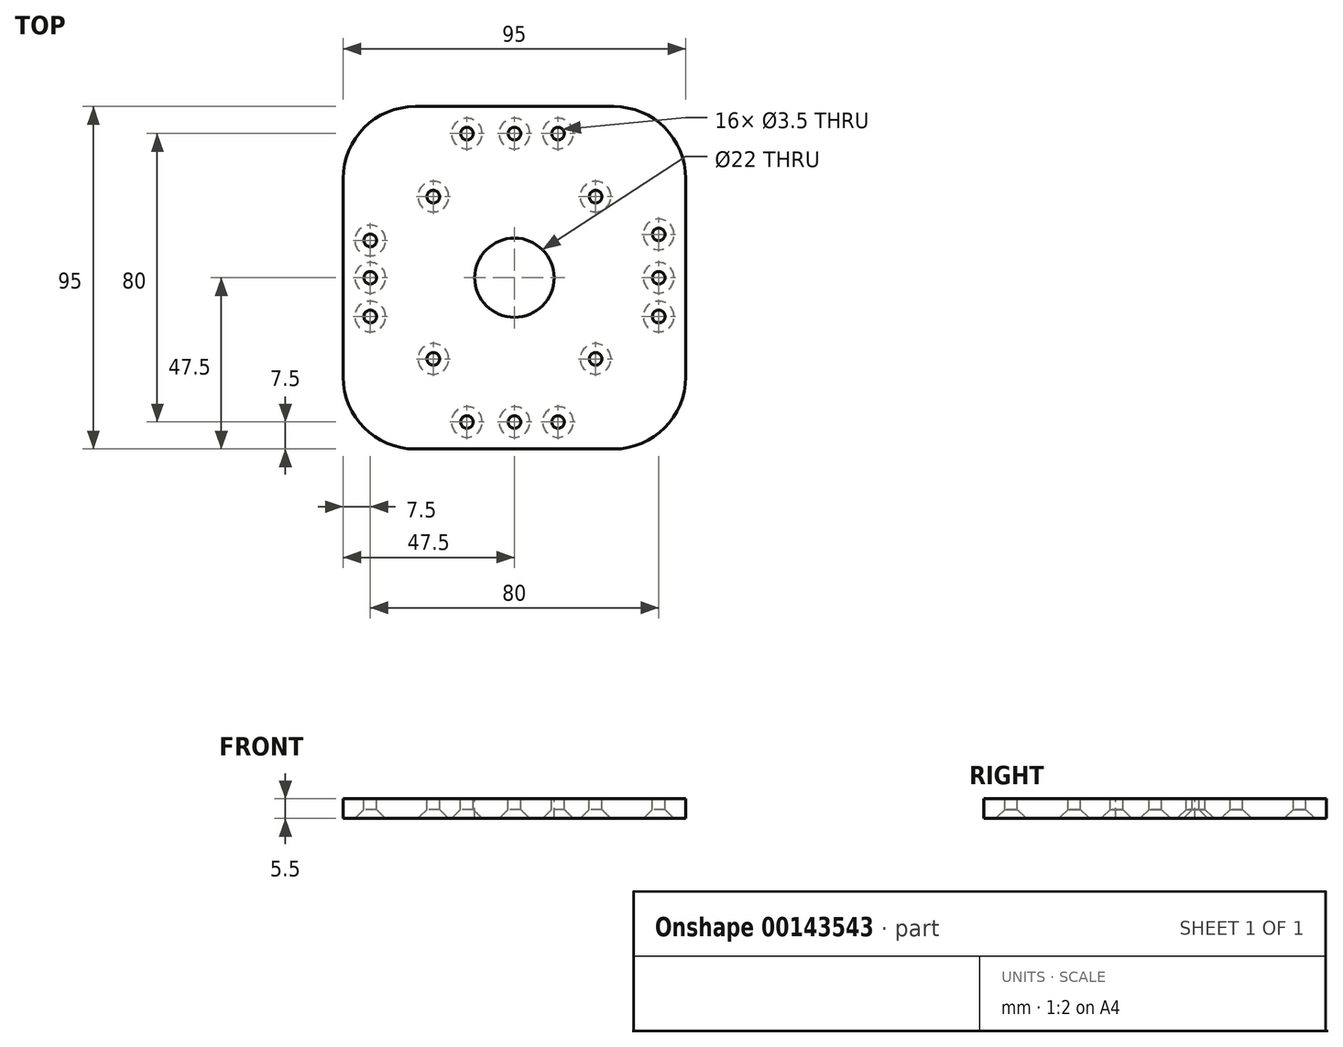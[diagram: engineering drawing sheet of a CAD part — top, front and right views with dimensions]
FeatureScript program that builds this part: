
annotation { "Feature Type Name" : "Feature", "Feature Type Description" : "" }
export const myFeature = defineFeature(function(context is Context, id is Id, definition is map)
    precondition{}
    {
        {
            var Q0;
            Q0=qCreatedBy(makeId("Top.planeOp"),FACE);
            var sketch = newSketch(context, id + "F0", { "sketchPlane" : qUnion([Q0])});
            skLineSegment(sketch, "E0.bottom", {"start": v(-47.5, 47.5) * mm, "end": v(47.5, 47.5) * mm});
            skLineSegment(sketch, "E0.top", {"start": v(-47.5, -47.5) * mm, "end": v(47.5, -47.5) * mm});
            skLineSegment(sketch, "E0.left", {"start": v(-47.5, 47.5) * mm, "end": v(-47.5, -47.5) * mm});
            skLineSegment(sketch, "E0.right", {"start": v(47.5, 47.5) * mm, "end": v(47.5, -47.5) * mm});
            skSolve(sketch);
        }
        {
            var Q0;
            Q0=makeQuery(id+"F0.imprint","IMPRINT",FACE,{"disambiguationData":[TD([[makeQuery(id+"F0.imprint","IMPRINT",EDGE,{"derivedFrom":sQuery(id+"F0.wireOp",EDGE,"E0.bottom")}),-1.0]])]});
            extrude(context, id + "F1", {"entities" : qUnion([Q0]), "depth" : 5.5 * mm});
        }
        {
            var Q0;
            Q0=makeQuery(id+"F1.opExtrude","SWEPT_EDGE",EDGE,{"disambiguationData":[OSD([sQuery(id+"F0.wireOp",EDGE,"E0.top"),sQuery(id+"F0.wireOp",EDGE,"E0.right")])]});
            var Q1;
            Q1=makeQuery(id+"F1.opExtrude","SWEPT_EDGE",EDGE,{"disambiguationData":[OSD([sQuery(id+"F0.wireOp",EDGE,"E0.bottom"),sQuery(id+"F0.wireOp",EDGE,"E0.right")])]});
            var Q2;
            Q2=makeQuery(id+"F1.opExtrude","SWEPT_EDGE",EDGE,{"disambiguationData":[OSD([sQuery(id+"F0.wireOp",EDGE,"E0.bottom"),sQuery(id+"F0.wireOp",EDGE,"E0.left")])]});
            var Q3;
            Q3=makeQuery(id+"F1.opExtrude","SWEPT_EDGE",EDGE,{"disambiguationData":[OSD([sQuery(id+"F0.wireOp",EDGE,"E0.top"),sQuery(id+"F0.wireOp",EDGE,"E0.left")])]});
            fillet(context, id + "F2", {"entities" : qUnion([Q0, Q1, Q2, Q3]), "radius" : 20 * mm, "tangentPropagation" : true, "allowEdgeOverflow" : false});
        }
        {
            var Q0;
            Q0=makeQuery(id+"F1.opExtrude","CAP_FACE",FACE,{"disambiguationData":[OSD([sQuery(id+"F0.wireOp",EDGE,"E0.bottom"),sQuery(id+"F0.wireOp",EDGE,"E0.top"),sQuery(id+"F0.wireOp",EDGE,"E0.left"),sQuery(id+"F0.wireOp",EDGE,"E0.right")])],"isStart":false});
            var sketch = newSketch(context, id + "F3", { "sketchPlane" : qUnion([Q0])});
            skCircle(sketch, "E1", {"center": v(0, 0) * mm, "radius": 11 * mm});
            skPoint(sketch, "E2", {"position": v(0, 40) * mm});
            skPoint(sketch, "E3", {"position": v(-40, 0) * mm});
            skPoint(sketch, "E4", {"position": v(0, -40) * mm});
            skPoint(sketch, "E5", {"position": v(40, 0) * mm});
            skSolve(sketch);
        }
        {
            var Q0;
            Q0 = qSketchRegion(id + "F3", true);
            extrude(context, id + "F4", {"entities" : qUnion([Q0]), "operationType" : NewBodyOperationType.REMOVE, "oppositeDirection" : true, "depth" : 5.5 * mm});
        }
        {
            var Q0;
            Q0=makeQuery(id+"F1.opExtrude","CAP_FACE",FACE,{"disambiguationData":[OSD([sQuery(id+"F0.wireOp",EDGE,"E0.bottom"),sQuery(id+"F0.wireOp",EDGE,"E0.top"),sQuery(id+"F0.wireOp",EDGE,"E0.left"),sQuery(id+"F0.wireOp",EDGE,"E0.right")])],"isStart":true});
            var sketch = newSketch(context, id + "F5", { "sketchPlane" : qUnion([Q0])});
            skPoint(sketch, "E6", {"position": v(0, 40) * mm});
            skPoint(sketch, "E7", {"position": v(40, 0) * mm});
            skPoint(sketch, "E8", {"position": v(-40, 0) * mm});
            skPoint(sketch, "E9", {"position": v(0, -40) * mm});
            skSolve(sketch);
        }
        {
            var Q0;
            Q0=sQuery(id+"F5.wireOp",VERTEX,"E9");
            var Q1;
            Q1=sQuery(id+"F5.wireOp",VERTEX,"E6");
            var Q2;
            Q2=sQuery(id+"F5.wireOp",VERTEX,"E7");
            var Q3;
            Q3=sQuery(id+"F5.wireOp",VERTEX,"E8");
            var Q4;
            Q4=makeQuery(id+"F1.opExtrude","SWEPT_BODY",BODY,{"disambiguationData":[OSD([sQuery(id+"F0.wireOp",EDGE,"E0.bottom"),sQuery(id+"F0.wireOp",EDGE,"E0.top"),sQuery(id+"F0.wireOp",EDGE,"E0.left"),sQuery(id+"F0.wireOp",EDGE,"E0.right")])]});
            hole(context, id + "F6", {"style" : HoleStyle.C_SINK, "endStyle" : HoleEndStyle.THROUGH, "holeDiameter" : 3.5 * mm, "cSinkDiameter" : 8.5 * mm, "cSinkAngle" : 90 * degree, "locations" : qUnion([Q0, Q1, Q2, Q3]), "scope" : qUnion([Q4]), "isTappedThrough" : true, "startStyle" : HoleStartStyle.SKETCH});
        }
        {
            var Q0;
            Q0=makeQuery(id+"F1.opExtrude","CAP_FACE",FACE,{"disambiguationData":[OSD([sQuery(id+"F0.wireOp",EDGE,"E0.bottom"),sQuery(id+"F0.wireOp",EDGE,"E0.top"),sQuery(id+"F0.wireOp",EDGE,"E0.left"),sQuery(id+"F0.wireOp",EDGE,"E0.right")])],"isStart":true});
            var sketch = newSketch(context, id + "F7", { "sketchPlane" : qUnion([Q0])});
            skPoint(sketch, "E10", {"position": v(12.09, 40) * mm});
            skPoint(sketch, "E11", {"position": v(-13.19, 40) * mm});
            skPoint(sketch, "E12", {"position": v(12.09, -40) * mm});
            skPoint(sketch, "E13", {"position": v(-13.19, -40) * mm});
            skPoint(sketch, "E14", {"position": v(40, 10.75) * mm});
            skPoint(sketch, "E15", {"position": v(-40, 10.75) * mm});
            skPoint(sketch, "E16", {"position": v(-40, -10.35) * mm});
            skPoint(sketch, "E17", {"position": v(40, -12.02) * mm});
            skSolve(sketch);
        }
        {
            var Q0;
            Q0=sQuery(id+"F7.wireOp",VERTEX,"E11");
            var Q1;
            Q1=sQuery(id+"F7.wireOp",VERTEX,"E10");
            var Q2;
            Q2=sQuery(id+"F7.wireOp",VERTEX,"E14");
            var Q3;
            Q3=sQuery(id+"F7.wireOp",VERTEX,"E17");
            var Q4;
            Q4=sQuery(id+"F7.wireOp",VERTEX,"E12");
            var Q5;
            Q5=sQuery(id+"F7.wireOp",VERTEX,"E13");
            var Q6;
            Q6=sQuery(id+"F7.wireOp",VERTEX,"E16");
            var Q7;
            Q7=sQuery(id+"F7.wireOp",VERTEX,"E15");
            var Q8;
            Q8=makeQuery(id+"F1.opExtrude","SWEPT_BODY",BODY,{"disambiguationData":[OSD([sQuery(id+"F0.wireOp",EDGE,"E0.bottom"),sQuery(id+"F0.wireOp",EDGE,"E0.top"),sQuery(id+"F0.wireOp",EDGE,"E0.left"),sQuery(id+"F0.wireOp",EDGE,"E0.right")])]});
            hole(context, id + "F8", {"style" : HoleStyle.C_SINK, "endStyle" : HoleEndStyle.THROUGH, "holeDiameter" : 3.5 * mm, "cSinkDiameter" : 8.5 * mm, "cSinkAngle" : 90 * degree, "locations" : qUnion([Q0, Q1, Q2, Q3, Q4, Q5, Q6, Q7]), "scope" : qUnion([Q8]), "isTappedThrough" : true, "startStyle" : HoleStartStyle.SKETCH});
        }
        {
            var Q0;
            Q0=makeQuery(id+"F1.opExtrude","CAP_FACE",FACE,{"disambiguationData":[OSD([sQuery(id+"F0.wireOp",EDGE,"E0.bottom"),sQuery(id+"F0.wireOp",EDGE,"E0.top"),sQuery(id+"F0.wireOp",EDGE,"E0.left"),sQuery(id+"F0.wireOp",EDGE,"E0.right")])],"isStart":true});
            var sketch = newSketch(context, id + "F9", { "sketchPlane" : qUnion([Q0])});
            skPoint(sketch, "E18", {"position": v(-22.5, -22.5) * mm});
            skPoint(sketch, "E19", {"position": v(22.5, -22.5) * mm});
            skPoint(sketch, "E20", {"position": v(22.5, 22.5) * mm});
            skPoint(sketch, "E21", {"position": v(-22.5, 22.5) * mm});
            skSolve(sketch);
        }
        {
            var Q0;
            Q0=sQuery(id+"F9.wireOp",VERTEX,"E21");
            var Q1;
            Q1=sQuery(id+"F9.wireOp",VERTEX,"E20");
            var Q2;
            Q2=sQuery(id+"F9.wireOp",VERTEX,"E19");
            var Q3;
            Q3=sQuery(id+"F9.wireOp",VERTEX,"E18");
            var Q4;
            Q4=makeQuery(id+"F1.opExtrude","SWEPT_BODY",BODY,{"disambiguationData":[OSD([sQuery(id+"F0.wireOp",EDGE,"E0.bottom"),sQuery(id+"F0.wireOp",EDGE,"E0.top"),sQuery(id+"F0.wireOp",EDGE,"E0.left"),sQuery(id+"F0.wireOp",EDGE,"E0.right")])]});
            hole(context, id + "F10", {"style" : HoleStyle.C_SINK, "endStyle" : HoleEndStyle.THROUGH, "holeDiameter" : 3.5 * mm, "cSinkDiameter" : 8.5 * mm, "cSinkAngle" : 90 * degree, "locations" : qUnion([Q0, Q1, Q2, Q3]), "scope" : qUnion([Q4]), "isTappedThrough" : true, "startStyle" : HoleStartStyle.SKETCH});
        }
    });
